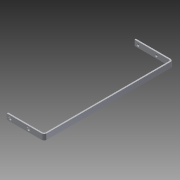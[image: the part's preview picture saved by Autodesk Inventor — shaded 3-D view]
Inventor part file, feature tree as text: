
AUTODESK INVENTOR PART (.ipt)
format: ipt  version: 2013 (Build 170138000, 138)  size: 115,712 bytes
history: native  units: in
note: dims shown in document units (in); Inventor stores cm internally (conversion verified against a paired STEP export)
features: sheet_metal_op x7, other x3, sketch x3, reference x2, extrude x1
ambient origin geometry x8: Origin, YZ Plane, XZ Plane, XY Plane, X Axis, Y Axis, Z Axis, Center Point
feature tree (16):
  sheet_metal_op  "Face2"
  sheet_metal_op  "Flange4"
  sheet_metal_op  "Flange5"
  extrude  "Extrusion2"  Depth=0.5in
  other  "Plate5"
  sketch  "Sketch6"  dims[d1=3.119in d2=0.5in]
  other  "Plate6"
  sheet_metal_op  "Bend4"
  sheet_metal_op  "Corner4"
  sketch  "Sketch7"  dims[d5=0.295in]
  other  "Plate7"
  sheet_metal_op  "Bend5"
  sheet_metal_op  "Corner5"
  sketch  "Sketch8"  dims[d8=0.125in d42=0.125in d43=0.125in d44=0.0625in d45=0.25in d46=0.125in d47=11.393in d48=90.0deg d49=0.125in d50=0.5in d51=0.125in d52=0.125in d53=0.125in d54=0.0625in d55=0.25in d56=0.125in d57=3.369in d58=90.0deg d59=0.125in d60=0.5in d61=0.125in d62=0.125in d63=99999.0in d64=0.0in]
  reference  "Reference1"
  reference  "Reference2"
